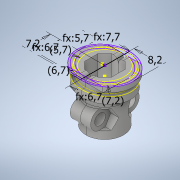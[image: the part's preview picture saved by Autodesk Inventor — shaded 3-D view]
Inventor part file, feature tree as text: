
AUTODESK INVENTOR PART (.ipt)
format: ipt  version: 2021.1 (Build 251245010, 245A)  size: 309,248 bytes
history: mixed  units: in
note: dims shown in document units (in); Inventor stores cm internally (conversion verified against a paired STEP export)
features: extrude x4, projected_geometry x4, sketch x3, other x2, imported_body x1
ambient origin geometry x8: Origin, YZ Plane, XZ Plane, XY Plane, X Axis, Y Axis, Z Axis, Center Point
bodies: Solid1 (imported_parasolid), Solid2 (imported_parasolid)
feature tree (14):
  other  "OBS-D-005"
  sketch  "Skizze1"  dims[d0=0.2638in d1=0.2244in]
  extrude  "Extrusion1"  Depth=0.2638in
  sketch  "Skizze4"  dims[d2=0.2244in d4=0.2835in]
  extrude  "Extrusion2"  Depth=0.2835in
  extrude  "Extrusion3"  Depth=0.3937in
  extrude  "Extrusion5"  Depth=0.3937in TaperAngle=0.0deg
  sketch  "Skizze6"  dims[d5=0.2835in d6=0.3228in d7=0.3937in d8=0.0in d12=0.2638in d13=0.2638in d14=0.3031in d15=0.3937in d16=0.0in d17=0.3937in d18=0.0in d21=0.3937in d22=0.0in]
  projected_geometry  "Projizierte Kontur1"
  projected_geometry  "Projizierte Kontur2"
  projected_geometry  "Projizierte Kontur3"
  projected_geometry  "Projizierte Kontur4"
  other  "OBS-D-004"
  imported_body  NMx_Import_Brep_tag  [imported B-rep: ~20 faces, bbox_mm=[7.935441, 12.75, 11.4]]
